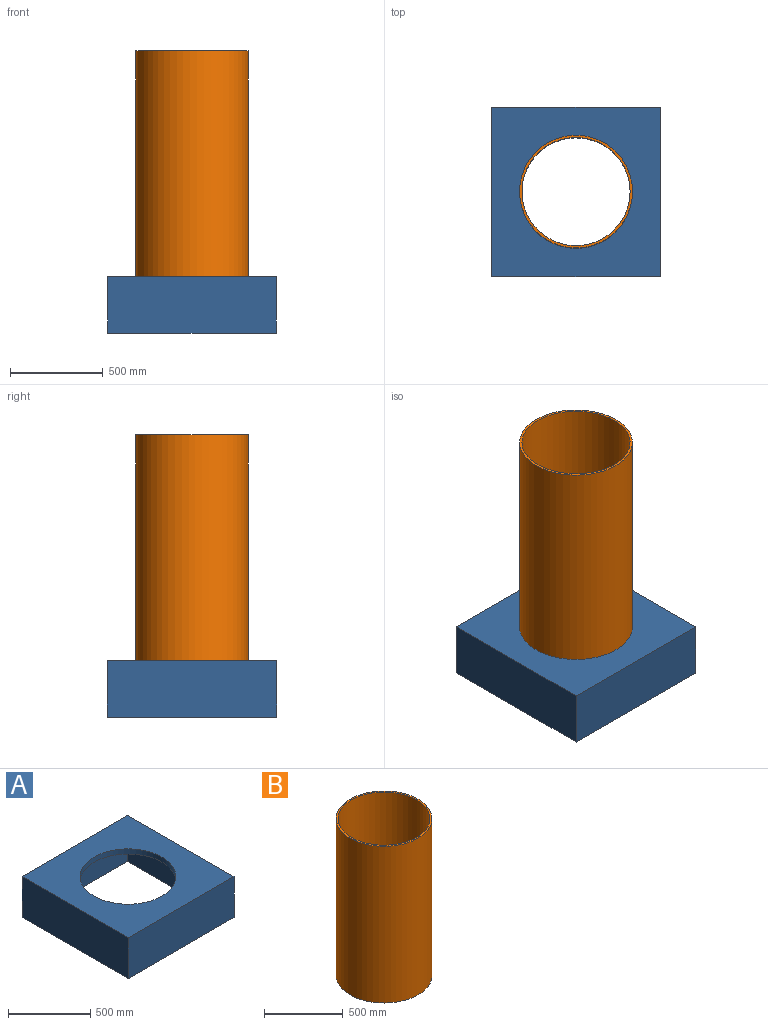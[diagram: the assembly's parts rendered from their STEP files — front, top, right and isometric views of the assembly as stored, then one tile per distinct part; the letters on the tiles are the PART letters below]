
ASSEMBLY  parts=2 mates=1
PART A: 12 faces, bbox 912.2x914.4x304.8 mm
  f0: plane 914.4x912.22mm, normal (0,0,-1), area 133381.8mm2, adj f1,f2,f3,f4,f6,f7,f8,f9
  f1: plane 914.4x304.8mm, normal (1,0,0), area 278709.1mm2, adj f0,f2,f4,f5
  f2: plane 912.22x304.8mm, normal (0,1,0), area 278044mm2, adj f0,f1,f3,f5
  f3: plane 914.4x304.8mm, normal (-1,0,0), area 278709.1mm2, adj f0,f2,f4,f5
  f4: plane 912.22x304.8mm, normal (0,-1,0), area 278044mm2, adj f0,f1,f3,f5
  f5: plane 914.4x912.22mm, normal (0,0,1), area 566083.6mm2, adj f1,f2,f3,f4,f11
  f6: plane 838.2x266.7mm, normal (-1,0,0), area 223547.9mm2, adj f0,f7,f9,f10
  f7: plane 836.02x266.7mm, normal (0,-1,0), area 222965.9mm2, adj f0,f6,f8,f10
  f8: plane 838.2x266.7mm, normal (1,0,0), area 223547.9mm2, adj f0,f7,f9,f10
  f9: plane 836.02x266.7mm, normal (0,1,0), area 222965.9mm2, adj f0,f6,f8,f10
  f10: plane 838.2x836.02mm, normal (0,0,-1), area 432701.8mm2, adj f6,f7,f8,f9,f11
  f11: cylinder r=292.1mm len=584.2mm, axis (0,0,1), area 69925.6mm2, adj f5,f10
PART B: 4 faces, bbox 609.6x609.6x1219.2 mm
  f0: cylinder r=304.8mm len=1219.2mm, axis (0,0,1), area 2334908.1mm2, adj f1,f2
  f1: plane 609.6x609.6mm, normal (0,0,-1), area 23815.3mm2, adj f0,f3
  f2: plane 609.6x609.6mm, normal (0,0,1), area 23815.3mm2, adj f0,f3
  f3: cylinder r=292.1mm len=1219.2mm, axis (0,0,1), area 2237620.2mm2, adj f1,f2
PLACE A t=(-147.96,-297.28,-167.27)mm
PLACE B t=(-147.96,-297.28,1051.93)mm
MATE cylindrical B.f0 <-> A.f11  axis (0,0,1) through (-147.96,-297.28,-167.27)mm
